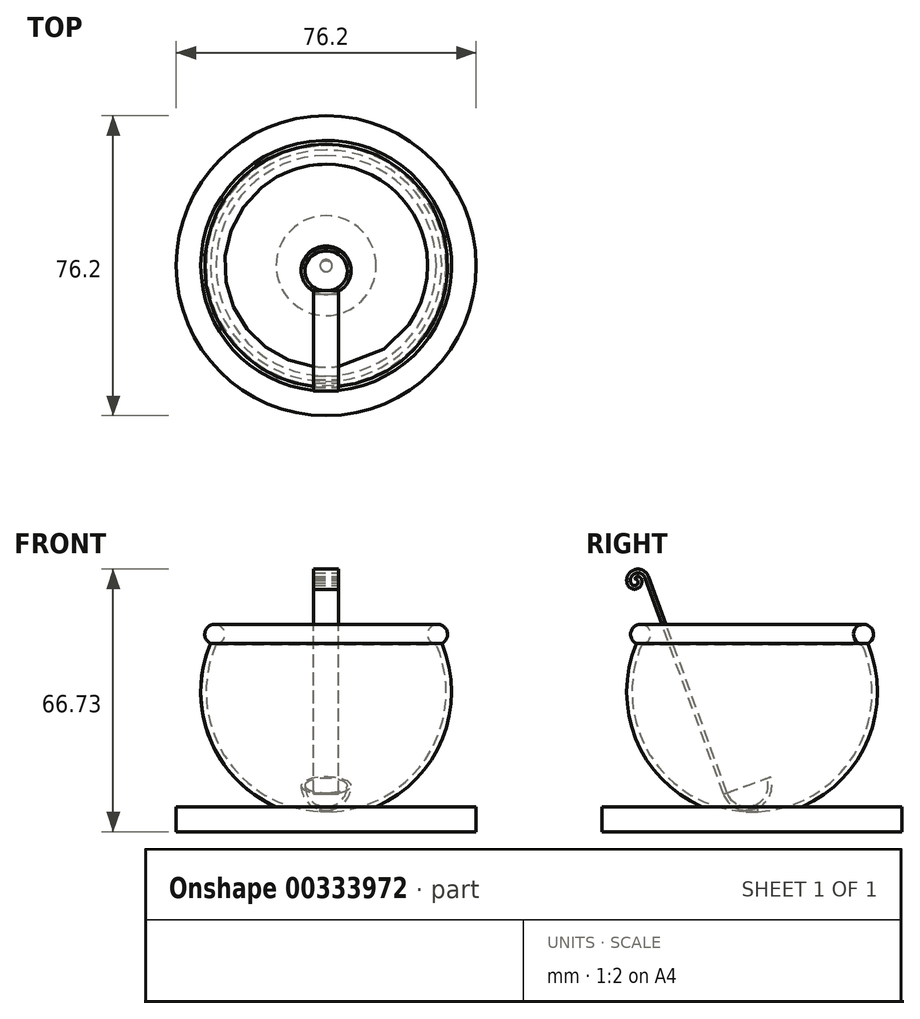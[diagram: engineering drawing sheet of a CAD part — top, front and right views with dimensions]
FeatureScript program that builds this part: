
annotation { "Feature Type Name" : "Feature", "Feature Type Description" : "" }
export const myFeature = defineFeature(function(context is Context, id is Id, definition is map)
    precondition{}
    {
        {
            var Q0;
            Q0=qCreatedBy(makeId("Top.planeOp"),FACE);
            var sketch = newSketch(context, id + "F0", { "sketchPlane" : qUnion([Q0])});
            skCircle(sketch, "E0", {"center": v(0, 0) * mm, "radius": 38.1 * mm});
            skSolve(sketch);
        }
        {
            var Q0;
            Q0=makeQuery(id+"F0.imprint","IMPRINT",FACE,{"disambiguationData":[TD([[makeQuery(id+"F0.imprint","IMPRINT",EDGE,{"derivedFrom":sQuery(id+"F0.wireOp",EDGE,"E0")}),1.0]])]});
            extrude(context, id + "F1", {"entities" : qUnion([Q0]), "depth" : 6.35 * mm});
        }
        {
            var Q0;
            Q0=qCreatedBy(makeId("Right.planeOp"),FACE);
            var sketch = newSketch(context, id + "F2", { "sketchPlane" : qUnion([Q0])});
            skLineSegment(sketch, "E1", {"start": v(0, 6.35) * mm, "end": v(-12.7, 6.35) * mm});
            skLineSegment(sketch, "E2", {"start": v(0, 6.35) * mm, "end": v(0, 35.56) * mm});
            skArc(sketch, "E3", {"start": v(-28.3, 50.16) * mm, "mid": v(-30, 24.87) * mm, "end": v(-12.7, 6.35) * mm});
            skLineSegment(sketch, "E4", {"start": v(0, 35.56) * mm, "end": v(0, 50.17) * mm});
            skLineSegment(sketch, "E5", {"start": v(0, 50.17) * mm, "end": v(-28.3, 50.17) * mm});
            skSolve(sketch);
        }
        {
            var Q0;
            Q0=makeQuery(id+"F2.imprint","IMPRINT",FACE,{"disambiguationData":[TD([[makeQuery(id+"F2.imprint","IMPRINT",EDGE,{"derivedFrom":sQuery(id+"F2.wireOp",EDGE,"E1")}),-1.0]])]});
            var Q1;
            Q1=sQuery(id+"F2.wireOp",EDGE,"E2");
            revolve(context, id + "F3", {"operationType" : NewBodyOperationType.ADD, "entities" : qUnion([Q0]), "axis" : qUnion([Q1]), "revolveType" : RevolveType.FULL});
        }
        {
            var Q0;
            Q0=qCreatedBy(makeId("Right.planeOp"),FACE);
            var sketch = newSketch(context, id + "F4", { "sketchPlane" : qUnion([Q0])});
            skPoint(sketch, "E6", {"position": v(0, 35.56) * mm});
            skArc(sketch, "E7", {"start": v(-26.35, 50.89) * mm, "mid": v(-26.42, 20.36) * mm, "end": v(0, 5.08) * mm});
            skLineSegment(sketch, "E8", {"start": v(0, 5.08) * mm, "end": v(0, 50.89) * mm});
            skLineSegment(sketch, "E9", {"start": v(0, 50.89) * mm, "end": v(-26.35, 50.89) * mm});
            skSolve(sketch);
        }
        {
            var Q0;
            Q0 = qSketchRegion(id + "F4", true);
            var Q1;
            Q1=sQuery(id+"F4.wireOp",EDGE,"E8");
            revolve(context, id + "F5", {"operationType" : NewBodyOperationType.REMOVE, "entities" : qUnion([Q0]), "axis" : qUnion([Q1]), "revolveType" : RevolveType.FULL, "oppositeDirection" : true});
        }
        {
            var Q0;
            Q0=qCreatedBy(makeId("Right.planeOp"),FACE);
            var sketch = newSketch(context, id + "F6", { "sketchPlane" : qUnion([Q0])});
            skCircle(sketch, "E10", {"center": v(-28.31, 50.17) * mm, "radius": 2.54 * mm});
            skSolve(sketch);
        }
        {
            var Q0;
            Q0=makeQuery(id+"F6.imprint","IMPRINT",FACE,{"disambiguationData":[TD([[makeQuery(id+"F6.imprint","IMPRINT",EDGE,{"derivedFrom":sQuery(id+"F6.wireOp",EDGE,"E10")}),1.0]])]});
            var Q1;
            Q1=sQuery(id+"F2.wireOp",EDGE,"E4");
            revolve(context, id + "F7", {"operationType" : NewBodyOperationType.ADD, "entities" : qUnion([Q0]), "axis" : qUnion([Q1]), "revolveType" : RevolveType.FULL});
        }
        {
            var Q0;
            Q0=qCreatedBy(makeId("Right.planeOp"),FACE);
            var sketch = newSketch(context, id + "F8", { "sketchPlane" : qUnion([Q0])});
            skPoint(sketch, "E11", {"position": v(0, 8.23) * mm});
            skLineSegment(sketch, "E12", {"start": v(-7.25, 9.6) * mm, "end": v(-22.47, 51.5) * mm});
            skLineSegment(sketch, "E13", {"start": v(-22.47, 51.5) * mm, "end": v(-27.2, 64.5) * mm});
            skArc(sketch, "E14", {"start": v(-27.2, 64.5) * mm, "mid": v(-29.64, 65.64) * mm, "end": v(-30.78, 63.2) * mm});
            skPoint(sketch, "E15", {"position": v(-29.88, 63.53) * mm});
            skArc(sketch, "E16", {"start": v(-30.78, 63.2) * mm, "mid": v(-29.55, 62.62) * mm, "end": v(-28.98, 63.85) * mm});
            skPoint(sketch, "E17", {"position": v(-28.09, 64.18) * mm});
            skArc(sketch, "E18", {"start": v(-31.67, 62.88) * mm, "mid": v(-29.23, 61.74) * mm, "end": v(-28.09, 64.18) * mm});
            skLineSegment(sketch, "E19", {"start": v(-28.98, 63.85) * mm, "end": v(-29.82, 64.3) * mm});
            skArc(sketch, "E20", {"start": v(-28.09, 64.18) * mm, "mid": v(-28.91, 64.82) * mm, "end": v(-29.82, 64.3) * mm});
            skLineSegment(sketch, "E21", {"start": v(-27.2, 64.5) * mm, "end": v(-26.3, 64.83) * mm});
            skArc(sketch, "E22", {"start": v(-26.3, 64.83) * mm, "mid": v(-29.97, 66.56) * mm, "end": v(-31.67, 62.88) * mm});
            skLineSegment(sketch, "E23", {"start": v(-7.25, 9.6) * mm, "end": v(-6.36, 9.92) * mm});
            skLineSegment(sketch, "E24", {"start": v(-6.36, 9.92) * mm, "end": v(-26.3, 64.83) * mm});
            skSolve(sketch);
        }
        {
            var Q0;
            Q0=makeQuery(id+"F8.imprint","IMPRINT",FACE,{"disambiguationData":[TD([[makeQuery(id+"F8.imprint","IMPRINT",EDGE,{"derivedFrom":sQuery(id+"F8.wireOp",EDGE,"E12")}),-1.0]])]});
            var Q1;
            Q1=makeQuery(id+"F8.imprint","IMPRINT",FACE,{"disambiguationData":[TD([[makeQuery(id+"F8.imprint","IMPRINT",EDGE,{"derivedFrom":sQuery(id+"F8.wireOp",EDGE,"E14")}),-1.0]])]});
            extrude(context, id + "F9", {"entities" : qUnion([Q0, Q1]), "endBound" : BoundingType.SYMMETRIC, "oppositeDirection" : true, "depth" : 6.35 * mm});
        }
        {
            var Q0;
            Q0=qCreatedBy(makeId("Right.planeOp"),FACE);
            var sketch = newSketch(context, id + "F10", { "sketchPlane" : qUnion([Q0])});
            skLineSegment(sketch, "E25", {"start": v(-7.29, 9.58) * mm, "end": v(-6.4, 9.9) * mm});
            skPoint(sketch, "E26", {"position": v(-1.32, 11.75) * mm});
            skArc(sketch, "E27", {"start": v(-7.29, 9.58) * mm, "mid": v(-4, 6) * mm, "end": v(0.85, 5.78) * mm});
            skPoint(sketch, "E28", {"position": v(-6.4, 9.9) * mm});
            skArc(sketch, "E29", {"start": v(-6.4, 9.9) * mm, "mid": v(-3.6, 6.86) * mm, "end": v(0.52, 6.67) * mm});
            skPoint(sketch, "E30", {"position": v(3.51, 9.34) * mm});
            skLineSegment(sketch, "E31", {"start": v(-1.32, 11.75) * mm, "end": v(0.52, 6.67) * mm});
            skLineSegment(sketch, "E32", {"start": v(0.52, 6.67) * mm, "end": v(0.85, 5.78) * mm});
            skSolve(sketch);
        }
        {
            var Q0;
            Q0=makeQuery(id+"F10.imprint","IMPRINT",FACE,{"disambiguationData":[TD([[makeQuery(id+"F10.imprint","IMPRINT",EDGE,{"derivedFrom":sQuery(id+"F10.wireOp",EDGE,"E25")}),-1.0]])]});
            var Q1;
            Q1=sQuery(id+"F10.wireOp",EDGE,"E31");
            revolve(context, id + "F11", {"operationType" : NewBodyOperationType.ADD, "entities" : qUnion([Q0]), "axis" : qUnion([Q1]), "revolveType" : RevolveType.FULL});
        }
        {
            var Q0;
            Q0=qCreatedBy(makeId("Right.planeOp"),FACE);
            var sketch = newSketch(context, id + "F12", { "sketchPlane" : qUnion([Q0])});
            skLineSegment(sketch, "E33", {"start": v(0, 4.2) * mm, "end": v(1.52, 4.2) * mm});
            skLineSegment(sketch, "E34", {"start": v(1.52, 4.2) * mm, "end": v(1.52, 5.91) * mm});
            skLineSegment(sketch, "E35", {"start": v(1.52, 5.91) * mm, "end": v(0, 5.94) * mm});
            skLineSegment(sketch, "E36", {"start": v(0, 5.94) * mm, "end": v(0, 4.2) * mm});
            skSolve(sketch);
        }
        {
            var Q0;
            Q0 = qSketchRegion(id + "F12", true);
            var Q1;
            Q1=sQuery(id+"F12.wireOp",EDGE,"E36");
            revolve(context, id + "F13", {"operationType" : NewBodyOperationType.ADD, "entities" : qUnion([Q0]), "axis" : qUnion([Q1]), "revolveType" : RevolveType.FULL});
        }
    });
